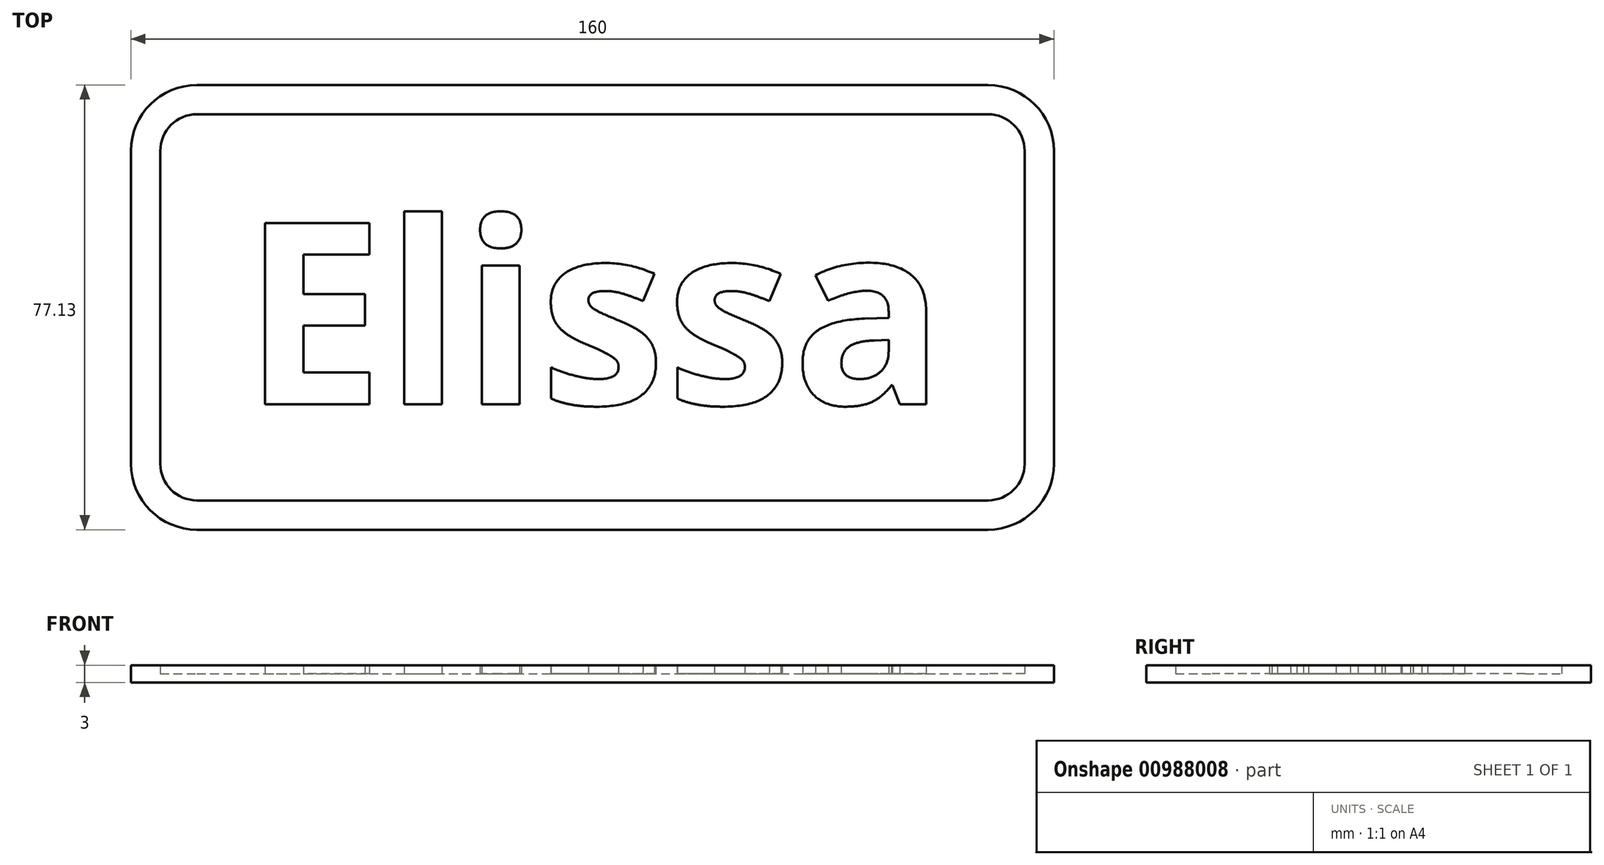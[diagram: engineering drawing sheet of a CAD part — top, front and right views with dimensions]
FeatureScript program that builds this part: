
annotation { "Feature Type Name" : "Feature", "Feature Type Description" : "" }
export const myFeature = defineFeature(function(context is Context, id is Id, definition is map)
    precondition{}
    {
        {
            var Q0;
            Q0=qCreatedBy(makeId("Top.planeOp"),FACE);
            var sketch = newSketch(context, id + "F0", { "sketchPlane" : qUnion([Q0])});
            skLineSegment(sketch, "E0.bottom", {"start": v(-68.57, 0) * mm, "end": v(68.57, 0) * mm});
            skLineSegment(sketch, "E0.top", {"start": v(-68.57, -66.97) * mm, "end": v(68.57, -66.97) * mm});
            skLineSegment(sketch, "E0.left", {"start": v(-74.92, -6.35) * mm, "end": v(-74.92, -60.62) * mm});
            skLineSegment(sketch, "E0.right", {"start": v(74.92, -6.35) * mm, "end": v(74.92, -60.62) * mm});
            skPoint(sketch, "E1.visualSharp", {"position": v(-74.92, 0) * mm});
            skArc(sketch, "E1.filletArc", {"start": v(-68.57, 0) * mm, "mid": v(-73.06, -1.86) * mm, "end": v(-74.92, -6.35) * mm});
            skPoint(sketch, "E2.visualSharp", {"position": v(74.92, 0) * mm});
            skArc(sketch, "E2.filletArc", {"start": v(74.92, -6.35) * mm, "mid": v(73.06, -1.86) * mm, "end": v(68.57, 0) * mm});
            skPoint(sketch, "E3.visualSharp", {"position": v(74.92, -66.97) * mm});
            skArc(sketch, "E3.filletArc", {"start": v(68.57, -66.97) * mm, "mid": v(73.06, -65.1) * mm, "end": v(74.92, -60.62) * mm});
            skPoint(sketch, "E4.visualSharp", {"position": v(-74.92, -66.97) * mm});
            skArc(sketch, "E4.filletArc", {"start": v(-74.92, -60.62) * mm, "mid": v(-73.06, -65.1) * mm, "end": v(-68.57, -66.97) * mm});
            skLineSegment(sketch, "E5.0", {"start": v(-68.57, -72.05) * mm, "end": v(68.57, -72.05) * mm});
            skArc(sketch, "E5.1", {"start": v(-80, -60.62) * mm, "mid": v(-76.65, -68.7) * mm, "end": v(-68.57, -72.05) * mm});
            skArc(sketch, "E5.2", {"start": v(68.57, -72.05) * mm, "mid": v(76.65, -68.7) * mm, "end": v(80, -60.62) * mm});
            skLineSegment(sketch, "E5.3", {"start": v(-80, -6.35) * mm, "end": v(-80, -60.62) * mm});
            skLineSegment(sketch, "E5.4", {"start": v(80, -6.35) * mm, "end": v(80, -60.62) * mm});
            skArc(sketch, "E5.5", {"start": v(80, -6.35) * mm, "mid": v(76.65, 1.73) * mm, "end": v(68.57, 5.08) * mm});
            skLineSegment(sketch, "E5.6", {"start": v(-68.57, 5.08) * mm, "end": v(68.57, 5.08) * mm});
            skArc(sketch, "E5.7", {"start": v(-68.57, 5.08) * mm, "mid": v(-76.65, 1.73) * mm, "end": v(-80, -6.35) * mm});
            skText(sketch, "E6", { "text": "Elissa", "fontName": "OpenSans-Bold.ttf"});
            const initialGuessF0  = {"E6": [-0.06072, -0.05028, 1, 0, 0.0317]};
            skSetInitialGuess(sketch, initialGuessF0);
            skSolve(sketch);
        }
        {
            var Q0;
            Q0=qCreatedBy(makeId("Top.planeOp"),FACE);
            var sketch = newSketch(context, id + "F1", { "sketchPlane" : qUnion([Q0])});
            skLineSegment(sketch, "E7.bottom", {"start": v(-75.87, 0) * mm, "end": v(75.87, 0) * mm});
            skLineSegment(sketch, "E7.top", {"start": v(-75.87, -68.16) * mm, "end": v(75.87, -68.16) * mm});
            skLineSegment(sketch, "E7.left", {"start": v(-75.87, 0) * mm, "end": v(-75.87, -68.16) * mm});
            skLineSegment(sketch, "E7.right", {"start": v(75.87, 0) * mm, "end": v(75.87, -68.16) * mm});
            skSolve(sketch);
        }
        {
            var Q0;
            Q0=makeQuery(id+"F0.imprint","IMPRINT",FACE,{"disambiguationData":[TD([[makeQuery(id+"F0.imprint","IMPRINT",EDGE,{"derivedFrom":sQuery(id+"F0.wireOp",EDGE,"E0.bottom")}),1.0]])]});
            var Q1;
            Q1=makeQuery(id+"F0.imprint","IMPRINT",FACE,{"disambiguationData":[TD([[makeQuery(id+"F0.imprint","IMPRINT",EDGE,{"derivedFrom":sQuery(id+"F0.wireOp",EDGE,"E6.sketch_text.stroke-0")}),-1.0]])]});
            var Q2;
            Q2=makeQuery(id+"F0.imprint","IMPRINT",FACE,{"disambiguationData":[TD([[makeQuery(id+"F0.imprint","IMPRINT",EDGE,{"derivedFrom":sQuery(id+"F0.wireOp",EDGE,"E6.sketch_text.stroke-12")}),-1.0]])]});
            var Q3;
            Q3=makeQuery(id+"F0.imprint","IMPRINT",FACE,{"disambiguationData":[TD([[makeQuery(id+"F0.imprint","IMPRINT",EDGE,{"derivedFrom":sQuery(id+"F0.wireOp",EDGE,"E6.sketch_text.stroke-21")}),-1.0]])]});
            var Q4;
            Q4=makeQuery(id+"F0.imprint","IMPRINT",FACE,{"disambiguationData":[TD([[makeQuery(id+"F0.imprint","IMPRINT",EDGE,{"derivedFrom":sQuery(id+"F0.wireOp",EDGE,"E6.sketch_text.stroke-16")}),-1.0]])]});
            var Q5;
            Q5=makeQuery(id+"F0.imprint","IMPRINT",FACE,{"disambiguationData":[TD([[makeQuery(id+"F0.imprint","IMPRINT",EDGE,{"derivedFrom":sQuery(id+"F0.wireOp",EDGE,"E6.sketch_text.stroke-25")}),-1.0]])]});
            var Q6;
            Q6=makeQuery(id+"F0.imprint","IMPRINT",FACE,{"disambiguationData":[TD([[makeQuery(id+"F0.imprint","IMPRINT",EDGE,{"derivedFrom":sQuery(id+"F0.wireOp",EDGE,"E6.sketch_text.stroke-51")}),-1.0]])]});
            var Q7;
            Q7=makeQuery(id+"F0.imprint","IMPRINT",FACE,{"disambiguationData":[TD([[makeQuery(id+"F0.imprint","IMPRINT",EDGE,{"derivedFrom":sQuery(id+"F0.wireOp",EDGE,"E6.sketch_text.stroke-77")}),-1.0]])]});
            extrude(context, id + "F2", {"entities" : qUnion([Q0, Q1, Q2, Q3, Q4, Q5, Q6, Q7]), "depth" : 3 * mm, "offsetDistance" : 25 * mm});
        }
        {
            var Q0;
            Q0=makeQuery(id+"F1.imprint","IMPRINT",FACE,{"disambiguationData":[TD([[makeQuery(id+"F1.imprint","IMPRINT",EDGE,{"derivedFrom":sQuery(id+"F1.wireOp",EDGE,"E7.bottom")}),-1.0]])]});
            extrude(context, id + "F3", {"entities" : qUnion([Q0]), "operationType" : NewBodyOperationType.ADD, "depth" : 1.5 * mm, "offsetDistance" : 25 * mm});
        }
    });
